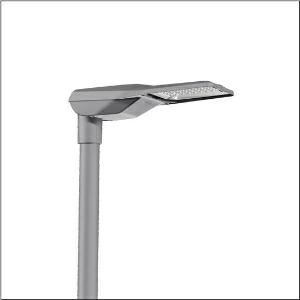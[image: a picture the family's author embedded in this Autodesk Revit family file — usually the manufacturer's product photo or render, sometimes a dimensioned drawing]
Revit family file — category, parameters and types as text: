
# Revit family: streetlight_sl_21_iq_mini___stw1_0a_5xe2e41d08gb_3fc6
name_source: partatom
category: Lighting Fixtures
units: mm (PartAtom-declared; Revit-internal decimal feet)

## family parameters
Cut with Voids When Loaded = No
Host = Face
Light Source = No
Part Type = Normal
Room Calculation Point = No
Round Connector Dimension = Use Diameter
Shared = No

## types (1)
- --- (1 x LED, 5920 lm, 37.1 W, 4000K)
    Apparent Load = 37 VA
    CIE Flux Codes = 38 75 98 100 100
    Color Rendering = 70
    Color Temperature = 4000K
    Default Elevation = 1800 mm
    Description = Streetlight SL 21 iQ mini, mast luminaire, primary light control with lens, of PMMA, primary optical cover: cover, of toughened safety glass, transparent, light distribution: STW1.0a, light emission: direct distribution, primary light characteristic: asymmetric, installation type: post-top, side-entry, LED, High Power LED, rated luminous flux: 5.920lm, luminous efficacy: 160lm/W, light colour: 740, colour temperature: 4000K, control: Auto-Match, Temp-Guard, Lumen-Switch, Night-Set, Smart-Wire, Light-Fading, Desk-Remote (wireless, voltage-free reading and setting of iQ features in the workshop via application-optimized NFC function/RFID function), optimised constant luminous flux control (CLO 2.0), presetting dimming linear, mains connection: 220..240V, AC, 50/60Hz, start of lifetime: 37W, end of service life: 39W, reduction: 18W, luminaire housing, of diecast aluminium, powder-coated, Siteco® metallic grey (DB 702S), corrosivity category C5 mid according to DIN EN ISO 12944, please order mast flange separately, inclination adjustable: 0°, 5°, 10°, 15°, sealing non-destructively replaceable, multi-level sealing system, length: 628mm, width: 235mm, height: 110mm, mast flange for spigot size: 42mm (side-entry): 5XC10008XM4, 60/48mm (side-entry/post-top): 5XC10108XM2, 76/60mm (side-entry/post-top): 5XC10108XM1, protection rating (complete): IP66, insulation class (complete): insulation class II (safety insulation), certification: CE, ENEC, ENEC+, VDE, impact resistance: IK09, permissible operating ambient temperature for outdoor applications: -40..+50°C, standard-compliant lighting for roads and squares, packaging unit: 1 piece

Light Distribution: STW1.0a
    Height = 110 mm
    Lamp = 1 x LED
    Lamp Light Flux = 5920 lm
    Lamp Power = 37.1 W
    Lamp count = 1
    Length = 625 mm
    Luminous efficacy = 160 lm/W
    Manufacturer = Siteco
    ModVariant = No
    Model = 5XE2E41D08GB
    Number of Poles = 1
    OnlyDefault = Yes
    Power Factor = 1
    Product Name = Streetlight SL 21 iQ mini | STW1.0a
    Product group = mast luminaire | pylon top
    ProductGroupID = 6100
    Protection Class = Protection class II
    Protection Degree = IP 66
    RLX_Detail_Level = 1
    RLX_Emergency_Light_Flux = 0 lm
    RLX_Emergency_Type = 0
    RLX_Emergency_Type_DB = No
    RlxData = <blob elided: 93537 chars, md5=33bb4613>
    Socket = socket
    Standby Power = 0 W
    System Light Flux = 5920 lm
    System Power = 37 W
    Type Comments = factory setting: luminous flux: 100 % | dim-lin: 254 | 385 mA
    Type Image = l_1003519.jpg
    URL = http://relux.com
    VarID = @adj_121019
    Voltage = 0 V
    Weight = 0.00 kg
    Width = 234 mm

## geometry (parser evidence)
native form markers: Blend x4, Sweep x12
no freeform markers — native parametric forms only
